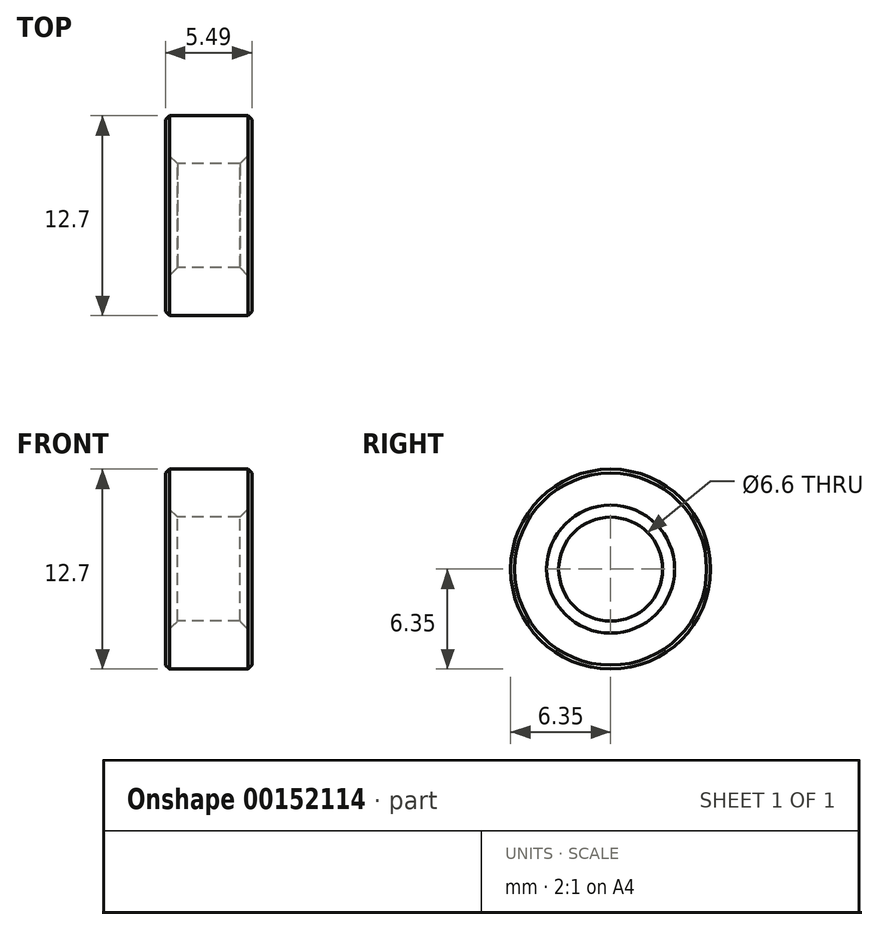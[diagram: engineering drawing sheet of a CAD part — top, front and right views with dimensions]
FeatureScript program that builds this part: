
annotation { "Feature Type Name" : "Feature", "Feature Type Description" : "" }
export const myFeature = defineFeature(function(context is Context, id is Id, definition is map)
    precondition{}
    {
        {
            var Q0;
            Q0=qCreatedBy(makeId("Right.planeOp"),FACE);
            var sketch = newSketch(context, id + "F0", { "sketchPlane" : qUnion([Q0])});
            skCircle(sketch, "E0", {"center": v(0, 0) * mm, "radius": 6.35 * mm});
            skCircle(sketch, "E1", {"center": v(0, 0) * mm, "radius": 3.3 * mm});
            skSolve(sketch);
        }
        {
            var Q0;
            Q0=makeQuery(id+"F0.imprint","IMPRINT",FACE,{"disambiguationData":[TD([[makeQuery(id+"F0.imprint","IMPRINT",EDGE,{"derivedFrom":sQuery(id+"F0.wireOp",EDGE,"E0")}),1.0]])]});
            extrude(context, id + "F1", {"entities" : qUnion([Q0]), "depth" : 5.5 * mm});
        }
        {
            var Q0;
            Q0=makeQuery(id+"F1.opExtrude","CAP_EDGE",EDGE,{"disambiguationData":[OSD([sQuery(id+"F0.wireOp",EDGE,"E1")])],"isStart":false});
            var Q1;
            Q1=makeQuery(id+"F1.opExtrude","CAP_EDGE",EDGE,{"disambiguationData":[OSD([sQuery(id+"F0.wireOp",EDGE,"E1")])],"isStart":true});
            chamfer(context, id + "F2", {"entities" : qUnion([Q0, Q1]), "width" : 0.76 * mm, "tangentPropagation" : true});
        }
        {
            var Q0;
            Q0=makeQuery(id+"F1.opExtrude","CAP_EDGE",EDGE,{"disambiguationData":[OSD([sQuery(id+"F0.wireOp",EDGE,"E0")])],"isStart":true});
            var Q1;
            Q1=makeQuery(id+"F1.opExtrude","CAP_EDGE",EDGE,{"disambiguationData":[OSD([sQuery(id+"F0.wireOp",EDGE,"E0")])],"isStart":false});
            chamfer(context, id + "F3", {"entities" : qUnion([Q0, Q1]), "width" : 0.25 * mm, "tangentPropagation" : true});
        }
    });
